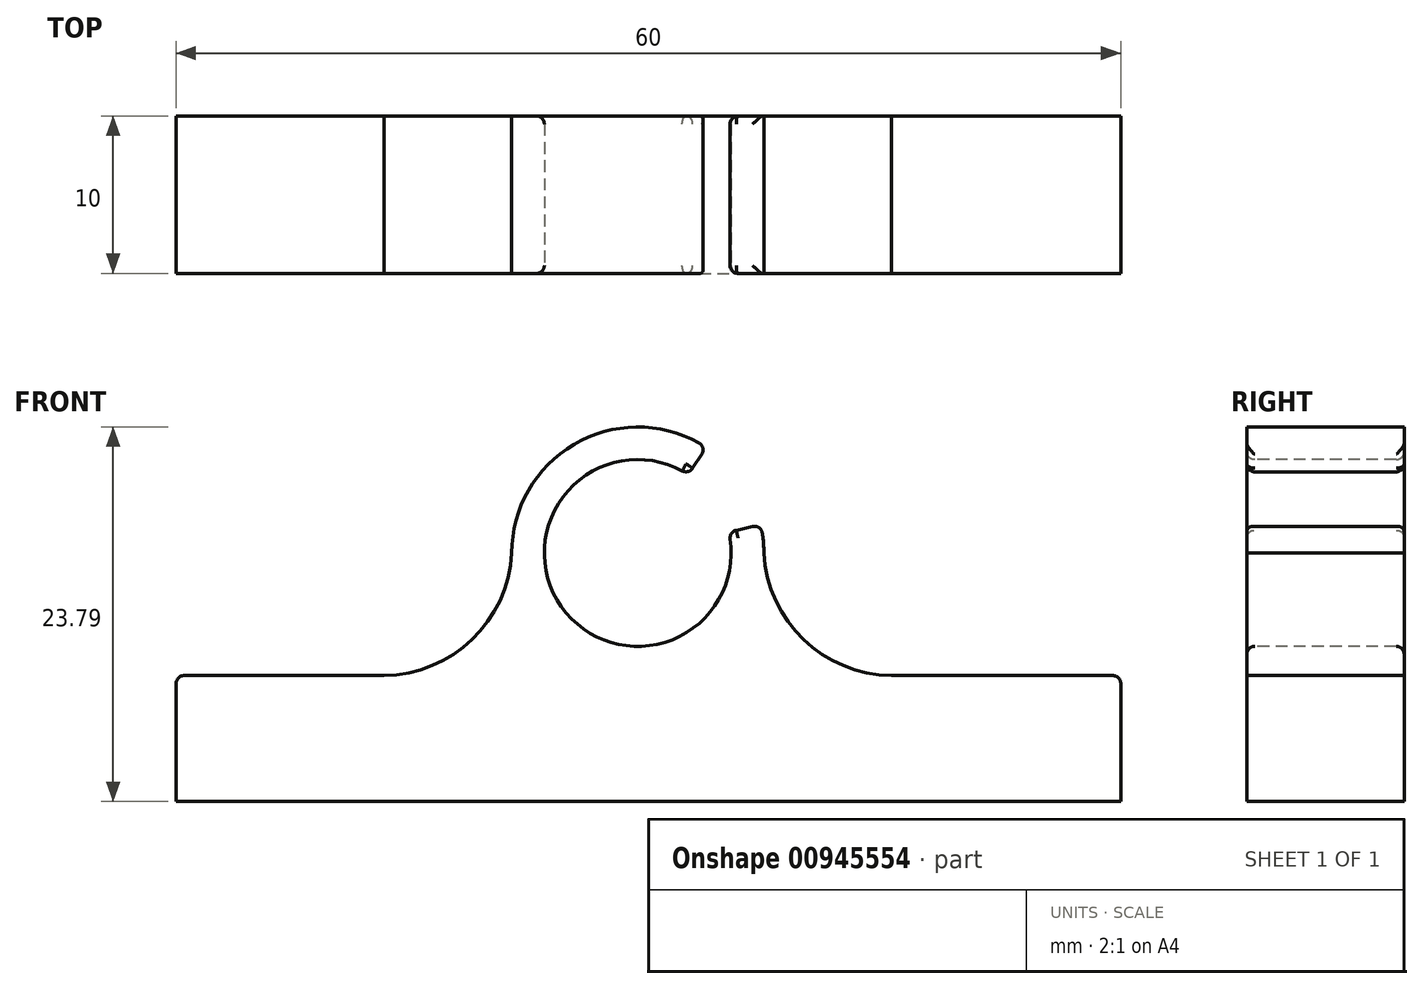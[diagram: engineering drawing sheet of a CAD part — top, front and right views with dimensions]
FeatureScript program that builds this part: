
annotation { "Feature Type Name" : "Feature", "Feature Type Description" : "" }
export const myFeature = defineFeature(function(context is Context, id is Id, definition is map)
    precondition{}
    {
        {
            var Q0;
            Q0=qCreatedBy(makeId("Top.planeOp"),FACE);
            var sketch = newSketch(context, id + "F0", { "sketchPlane" : qUnion([Q0])});
            skLineSegment(sketch, "E0", {"start": v(-29, 0) * mm, "end": v(31, 0) * mm});
            skLineSegment(sketch, "E1", {"start": v(-29, 0) * mm, "end": v(-29, -10) * mm});
            skLineSegment(sketch, "E2", {"start": v(31, 0) * mm, "end": v(31, -10) * mm});
            skLineSegment(sketch, "E3", {"start": v(31, -10) * mm, "end": v(-29, -10) * mm});
            skSolve(sketch);
        }
        {
            var Q0;
            Q0=makeQuery(id+"F0.imprint","IMPRINT",FACE,{"disambiguationData":[TD([[makeQuery(id+"F0.imprint","IMPRINT",EDGE,{"derivedFrom":sQuery(id+"F0.wireOp",EDGE,"E0")}),-1.0]])]});
            extrude(context, id + "F1", {"entities" : qUnion([Q0]), "depth" : 8 * mm, "offsetDistance" : 25.4 * mm});
        }
        {
            var Q0;
            Q0=makeQuery(id+"F1.opExtrude","SWEPT_FACE",FACE,{"disambiguationData":[OSD([sQuery(id+"F0.wireOp",EDGE,"E3")])]});
            var sketch = newSketch(context, id + "F2", { "sketchPlane" : qUnion([Q0])});
            skLineSegment(sketch, "E4", {"start": v(-29, 8) * mm, "end": v(31, 8) * mm});
            skArc(sketch, "E5", {"start": v(-16, 8) * mm, "mid": v(-10.28, 10.22) * mm, "end": v(-7.69, 15.79) * mm});
            skArc(sketch, "E6", {"start": v(3.54, 20.76) * mm, "mid": v(-4.54, 12.38) * mm, "end": v(6.1, 17.12) * mm});
            skArc(sketch, "E7", {"start": v(-7.69, 15.79) * mm, "mid": v(-3.5, 22.81) * mm, "end": v(4.67, 22.5) * mm});
            skLineSegment(sketch, "E8", {"start": v(4.67, 22.5) * mm, "end": v(3.54, 20.76) * mm});
            skLineSegment(sketch, "E9", {"start": v(8.12, 17.59) * mm, "end": v(6.1, 17.12) * mm});
            skArc(sketch, "E10", {"start": v(8.12, 17.59) * mm, "mid": v(8.27, 16.7) * mm, "end": v(8.32, 15.79) * mm});
            skArc(sketch, "E11", {"start": v(8.32, 15.79) * mm, "mid": v(10.84, 10.3) * mm, "end": v(16.43, 8) * mm});
            skSolve(sketch);
        }
        {
            var Q0;
            {var subQ1=sQuery(id+"F2.wireOp",EDGE,"E5");Q0=makeQuery(id+"F2.imprint","IMPRINT",FACE,{"disambiguationData":[TD([[makeQuery(id+"F2.imprint","IMPRINT",EDGE,{"derivedFrom":subQ1}),-1.0]])]});}
            extrude(context, id + "F3", {"entities" : qUnion([Q0]), "operationType" : NewBodyOperationType.ADD, "oppositeDirection" : true, "depth" : 10 * mm, "offsetDistance" : 25.4 * mm});
        }
        {
            var Q0;
            Q0=makeQuery(id+"F1.opExtrude","CAP_EDGE",EDGE,{"disambiguationData":[OSD([sQuery(id+"F0.wireOp",EDGE,"E2")])],"isStart":false});
            fillet(context, id + "F4", {"entities" : qUnion([Q0]), "tangentPropagation" : true, "radius" : 0.5 * mm, "defaultsChanged" : true, "vertexSettings" : [], "allowEdgeOverflow" : false});
        }
        {
            var Q0;
            Q0=makeQuery(id+"F1.opExtrude","CAP_EDGE",EDGE,{"disambiguationData":[OSD([sQuery(id+"F0.wireOp",EDGE,"E1")])],"isStart":false});
            fillet(context, id + "F5", {"entities" : qUnion([Q0]), "tangentPropagation" : true, "radius" : 0.5 * mm, "defaultsChanged" : true, "vertexSettings" : [], "allowEdgeOverflow" : false});
        }
        {
            var Q0;
            Q0=makeQuery(id+"F2.imprint","IMPRINT",FACE,{"disambiguationData":[TD([[makeQuery(id+"F2.imprint","IMPRINT",EDGE,{"derivedFrom":sQuery(id+"F2.wireOp",EDGE,"E6")}),-1.0]])]});
            extrude(context, id + "F6", {"entities" : qUnion([Q0]), "operationType" : NewBodyOperationType.ADD, "oppositeDirection" : true, "depth" : 10 * mm, "offsetDistance" : 25.4 * mm});
        }
        {
            var Q0;
            Q0=makeQuery(id+"F6.opExtrude","SWEPT_EDGE",EDGE,{"disambiguationData":[OSD([sQuery(id+"F2.wireOp",EDGE,"E7"),sQuery(id+"F2.wireOp",EDGE,"E8")])]});
            var Q1;
            Q1=makeQuery(id+"F6.opExtrude","SWEPT_EDGE",EDGE,{"disambiguationData":[OSD([sQuery(id+"F2.wireOp",EDGE,"E6"),sQuery(id+"F2.wireOp",EDGE,"E8")])]});
            var Q2;
            Q2=makeQuery(id+"F6.opExtrude","CAP_EDGE",EDGE,{"disambiguationData":[OSD([sQuery(id+"F2.wireOp",EDGE,"E8")])],"isStart":true});
            var Q3;
            Q3=makeQuery(id+"F6.opExtrude","CAP_EDGE",EDGE,{"disambiguationData":[OSD([sQuery(id+"F2.wireOp",EDGE,"E8")])],"isStart":false});
            var Q4;
            Q4=makeQuery(id+"F6.opExtrude","CAP_EDGE",EDGE,{"disambiguationData":[OSD([sQuery(id+"F2.wireOp",EDGE,"E9")])],"isStart":false});
            var Q5;
            Q5=makeQuery(id+"F6.opExtrude","SWEPT_EDGE",EDGE,{"disambiguationData":[OSD([sQuery(id+"F2.wireOp",EDGE,"E6"),sQuery(id+"F2.wireOp",EDGE,"E9")])]});
            var Q6;
            Q6=makeQuery(id+"F6.opExtrude","SWEPT_EDGE",EDGE,{"disambiguationData":[OSD([sQuery(id+"F2.wireOp",EDGE,"E9"),sQuery(id+"F2.wireOp",EDGE,"E10")])]});
            var Q7;
            Q7=makeQuery(id+"F6.opExtrude","CAP_EDGE",EDGE,{"disambiguationData":[OSD([sQuery(id+"F2.wireOp",EDGE,"E9")])],"isStart":true});
            fillet(context, id + "F7", {"entities" : qUnion([Q0, Q1, Q2, Q3, Q4, Q5, Q6, Q7]), "tangentPropagation" : true, "radius" : 0.5 * mm, "defaultsChanged" : true, "vertexSettings" : [], "allowEdgeOverflow" : false});
        }
        {
            var Q0;
            Q0=makeQuery(id+"F6.opExtrude","CAP_EDGE",EDGE,{"disambiguationData":[OSD([sQuery(id+"F2.wireOp",EDGE,"E6")])],"isStart":false});
            var Q1;
            Q1=makeQuery(id+"F6.opExtrude","CAP_EDGE",EDGE,{"disambiguationData":[OSD([sQuery(id+"F2.wireOp",EDGE,"E6")])],"isStart":true});
            fillet(context, id + "F8", {"entities" : qUnion([Q0, Q1]), "tangentPropagation" : true, "radius" : 0.5 * mm, "defaultsChanged" : true, "vertexSettings" : [], "allowEdgeOverflow" : false});
        }
    });
